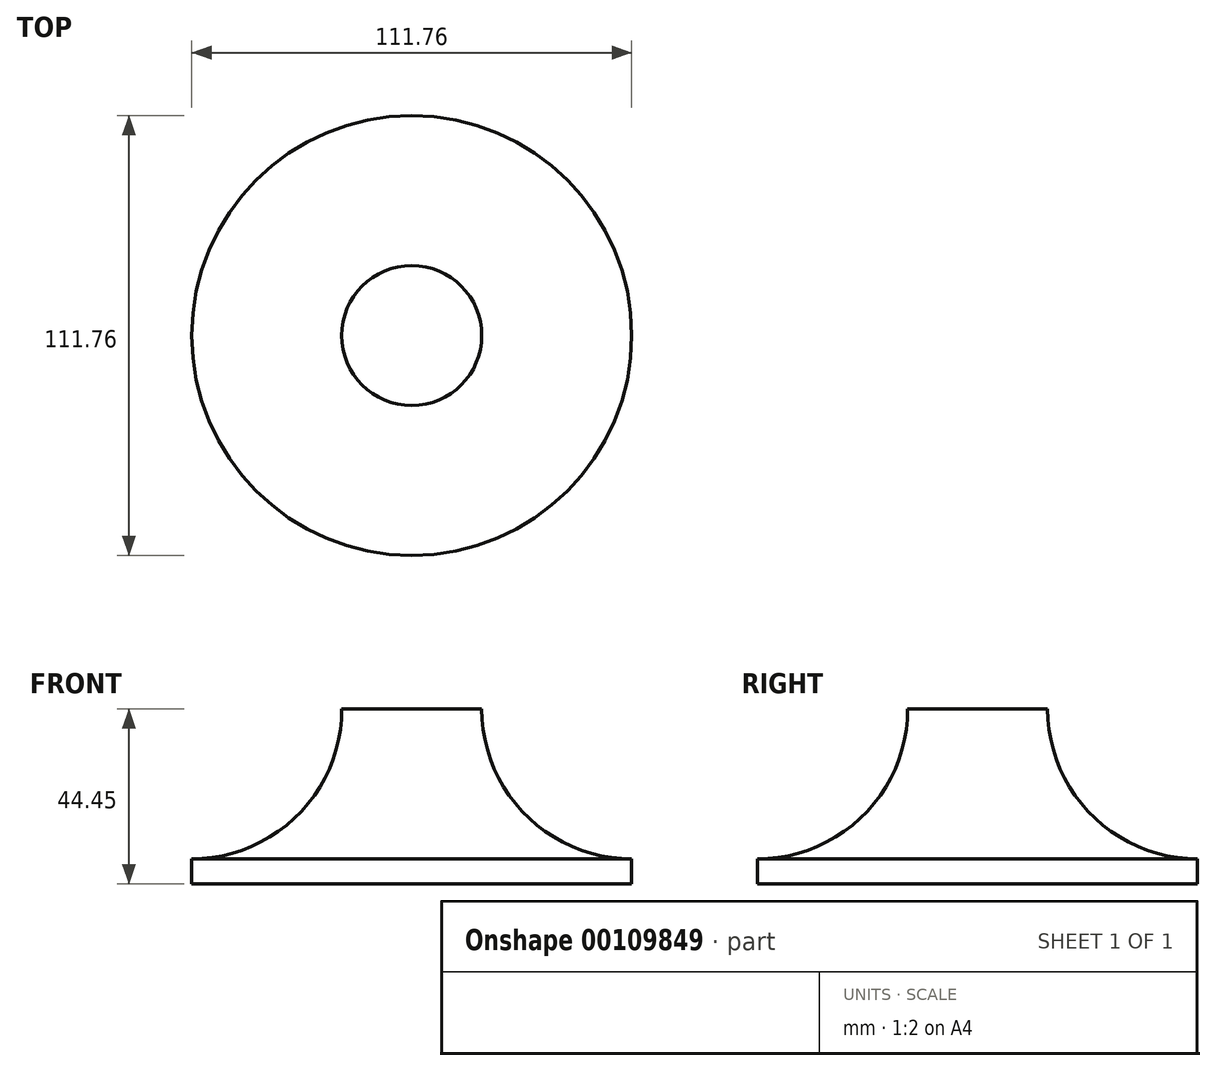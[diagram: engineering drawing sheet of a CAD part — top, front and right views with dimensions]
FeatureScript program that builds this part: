
annotation { "Feature Type Name" : "Feature", "Feature Type Description" : "" }
export const myFeature = defineFeature(function(context is Context, id is Id, definition is map)
    precondition{}
    {
        {
            var Q0;
            Q0=qCreatedBy(makeId("Right.planeOp"),FACE);
            var sketch = newSketch(context, id + "F0", { "sketchPlane" : qUnion([Q0])});
            skLineSegment(sketch, "E0", {"start": v(0, 0) * mm, "end": v(-55.88, 0) * mm});
            skLineSegment(sketch, "E1", {"start": v(-55.88, 0) * mm, "end": v(-55.88, 6.35) * mm});
            skArc(sketch, "E2", {"start": v(-55.88, 6.35) * mm, "mid": v(-28.94, 17.5) * mm, "end": v(-17.78, 44.45) * mm});
            skLineSegment(sketch, "E3", {"start": v(-17.78, 44.45) * mm, "end": v(0, 44.45) * mm});
            skLineSegment(sketch, "E4", {"start": v(0, 44.45) * mm, "end": v(0, 0) * mm});
            skLineSegment(sketch, "E5", {"start": v(-55.88, 44.45) * mm, "end": v(-55.88, 6.35) * mm, "construction": true});
            skLineSegment(sketch, "E6", {"start": v(-55.88, 44.45) * mm, "end": v(-17.78, 44.45) * mm, "construction": true});
            skSolve(sketch);
        }
        {
            var Q0;
            Q0 = qSketchRegion(id + "F0", true);
            var Q1;
            Q1=sQuery(id+"F0.wireOp",EDGE,"E4");
            revolve(context, id + "F1", {"entities" : qUnion([Q0]), "axis" : qUnion([Q1]), "revolveType" : RevolveType.FULL});
        }
        {
            var Q0;
            Q0=makeQuery(id+"F1.opRevolve","SWEPT_FACE",FACE,{"disambiguationData":[OSD([sQuery(id+"F0.wireOp",EDGE,"E3")])]});
            var sketch = newSketch(context, id + "F2", { "sketchPlane" : qUnion([Q0])});
            skArc(sketch, "E7", {"start": v(-3.06, -17.51) * mm, "mid": v(-9.7, -37.35) * mm, "end": v(0, -55.88) * mm});
            skArc(sketch, "E8", {"start": v(5.8, -16.8) * mm, "mid": v(-4.54, -36.94) * mm, "end": v(8.86, -55.17) * mm});
            skCircle(sketch, "E9.0", {"center": v(0, 0) * mm, "radius": 17.78 * mm});
            skCircle(sketch, "E10.0", {"center": v(0, 0) * mm, "radius": 55.88 * mm});
            skSolve(sketch);
        }
        {
            var Q0;
            {var subQ0=sQuery(id+"F2.wireOp",EDGE,"E9.0");var subQ1=makeQuery(id+"F2.imprint","INTERSECT",VERTEX,{"derivedFrom":[sQuery(id+"F2.wireOp",EDGE,"E7"),subQ0]});Q0=makeQuery(id+"F2.imprint","IMPRINT",FACE,{"disambiguationData":[TD([[makeQuery(id+"F2.imprint","IMPRINT",EDGE,{"disambiguationData":[TD([[subQ1,-1.0]])],"derivedFrom":subQ0}),1.0]])]});}
            var sketch = newSketch(context, id + "F3", { "sketchPlane" : qUnion([Q0])});
            skPoint(sketch, "E11.0", {"position": v(0, -55.88) * mm});
            skSolve(sketch);
        }
        {
            var Q0;
            Q0=qCreatedBy(makeId("Front.planeOp"),FACE);
            cPlane(context, id + "F4", {"entities" : qUnion([Q0]), "cplaneType" : CPlaneType.OFFSET, "offset" : 101.6 * mm, "width" : 152.4 * mm, "height" : 152.4 * mm});
        }
    });
